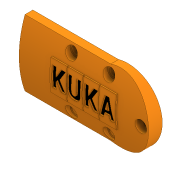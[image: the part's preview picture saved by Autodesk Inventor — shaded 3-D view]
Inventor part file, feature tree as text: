
AUTODESK INVENTOR PART (.ipt)
format: ipt  version: 2020 (Build 240168000, 168)  size: 518,656 bytes
history: native  units: in
note: dims shown in document units (in); Inventor stores cm internally (conversion verified against a paired STEP export)
features: sketch x12, extrude x11, plane x2, fillet x1, emboss x1, projected_geometry x1
ambient origin geometry x8: Origin, YZ Plane, XZ Plane, XY Plane, X Axis, Y Axis, Z Axis, Center Point
bodies: Solid1 (feature_tree)
feature tree (28):
  extrude  "Extrusion1"  Depth=0.2362in
  extrude  "Extrusion2"  Depth=0.2362in
  extrude  "Extrusion3"  Depth=0.2362in
  fillet  "Fillet1"  Radius=0.2264in
  plane  "Work Plane1"
  extrude  "Extrusion4"  Depth=0.1969in
  sketch  "Sketch5"  dims[d11=0.0in d12=0.0in d13=0.0787in]
  extrude  "Extrusion5"  Depth=0.0787in
  extrude  "Extrusion6"  Depth=0.5512in
  extrude  "Extrusion7"  Depth=0.9843in
  emboss  "Emboss1"
  plane  "Work Plane2"
  extrude  "Extrusion8"  Depth=0.0197in
  extrude  "Extrusion9"  Depth=0.0197in
  extrude  "Extrusion10"  Depth=0.0787in TaperAngle=0.0deg
  extrude  "Extrusion11"  Depth=0.0394in TaperAngle=0.0deg
  sketch  "Sketch1"  dims[d0=0.1575in d1=0.2362in]
  sketch  "Sketch2"  dims[d2=0.2362in d3=0.2362in]
  sketch  "Sketch3"  dims[d4=0.2362in d5=0.2362in d6=0.2264in d7=0.0in]
  sketch  "Sketch4"  dims[d8=0.1969in d9=0.0in d10=0.1969in]
  projected_geometry  "Projected Loop1"
  sketch  "Sketch6"  dims[d14=0.5512in d15=0.5512in]
  sketch  "Sketch7"  dims[d16=0.9843in d17=0.9843in]
  sketch  "Sketch8"  dims[d18=0.0787in d19=0.0in d20=0.0197in]
  sketch  "Sketch9"  dims[d21=0.0197in d22=0.0197in]
  sketch  "Sketch10"  dims[d23=0.0in d24=0.0in d25=0.0787in d26=0.0in]
  sketch  "Sketch11"  dims[d27=0.0in d28=0.0in d29=0.0394in d30=0.0in]
  sketch  "Sketch12"  dims[d31=0.3543in d32=0.3543in d33=0.3543in d34=0.3543in d35=0.3543in d36=0.4724in d37=0.0in d38=0.315in d39=0.5512in d40=0.0984in d41=0.0in d42=0.0984in d43=0.0in d44=0.2362in d45=0.0394in d46=0.0in]
